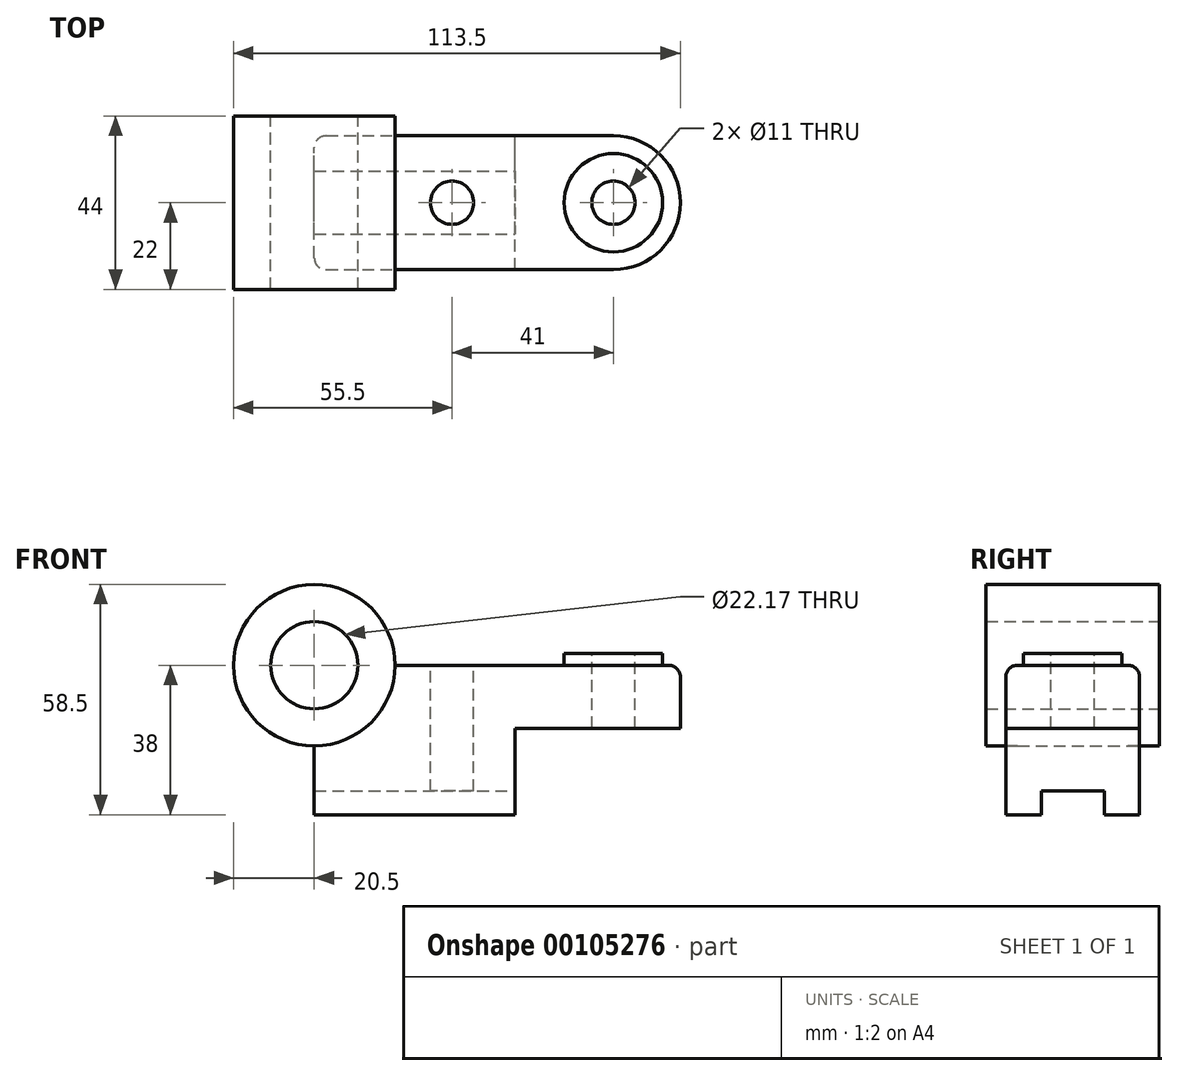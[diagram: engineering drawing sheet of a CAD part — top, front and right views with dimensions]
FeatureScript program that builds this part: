
annotation { "Feature Type Name" : "Feature", "Feature Type Description" : "" }
export const myFeature = defineFeature(function(context is Context, id is Id, definition is map)
    precondition{}
    {
        {
            var Q0;
            Q0=qCreatedBy(makeId("Front.planeOp"),FACE);
            var sketch = newSketch(context, id + "F0", { "sketchPlane" : qUnion([Q0])});
            skLineSegment(sketch, "E0.bottom", {"start": v(0, 0) * mm, "end": v(51, 0) * mm});
            skLineSegment(sketch, "E0.top", {"start": v(0, 38) * mm, "end": v(76, 38) * mm});
            skLineSegment(sketch, "E0.left", {"start": v(0, 0) * mm, "end": v(0, 38) * mm});
            skLineSegment(sketch, "E0.right", {"start": v(76, 22) * mm, "end": v(76, 38) * mm});
            skLineSegment(sketch, "E1.top", {"start": v(76, 22) * mm, "end": v(51, 22) * mm});
            skLineSegment(sketch, "E1.right", {"start": v(51, 0) * mm, "end": v(51, 22) * mm});
            skCircle(sketch, "E2", {"center": v(0, 38) * mm, "radius": 11.09 * mm});
            skCircle(sketch, "E3", {"center": v(0, 38) * mm, "radius": 20.5 * mm});
            skSolve(sketch);
        }
        {
            var Q0;
            {var subQ2=sQuery(id+"F0.wireOp",EDGE,"E0.bottom");Q0=makeQuery(id+"F0.imprint","IMPRINT",FACE,{"disambiguationData":[TD([[makeQuery(id+"F0.imprint","IMPRINT",EDGE,{"derivedFrom":subQ2}),1.0]])]});}
            extrude(context, id + "F1", {"entities" : qUnion([Q0]), "endBound" : BoundingType.SYMMETRIC, "depth" : (17 * 2) * mm});
        }
        {
            var Q0;
            {var subQ0=sQuery(id+"F0.wireOp",EDGE,"E3");var subQ1=sQuery(id+"F0.wireOp",EDGE,"E0.top");var subQ2=makeQuery(id+"F0.imprint","INTERSECT",VERTEX,{"derivedFrom":[subQ1,subQ0]});Q0=makeQuery(id+"F0.imprint","IMPRINT",FACE,{"disambiguationData":[TD([[makeQuery(id+"F0.imprint","IMPRINT",EDGE,{"disambiguationData":[TD([[subQ2,1.0]])],"derivedFrom":subQ1}),1.0]])]});}
            var Q1;
            {var subQ0=sQuery(id+"F0.wireOp",EDGE,"E3");var subQ1=sQuery(id+"F0.wireOp",EDGE,"E0.top");var subQ2=makeQuery(id+"F0.imprint","INTERSECT",VERTEX,{"derivedFrom":[subQ1,subQ0]});Q1=makeQuery(id+"F0.imprint","IMPRINT",FACE,{"disambiguationData":[TD([[makeQuery(id+"F0.imprint","IMPRINT",EDGE,{"disambiguationData":[TD([[subQ2,1.0]])],"derivedFrom":subQ1}),-1.0]])]});}
            extrude(context, id + "F2", {"entities" : qUnion([Q0, Q1]), "operationType" : NewBodyOperationType.ADD, "endBound" : BoundingType.SYMMETRIC, "depth" : 44 * mm});
        }
        {
            var Q0;
            Q0=makeQuery(id+"F1.opExtrude","SWEPT_FACE",FACE,{"disambiguationData":[OSD([sQuery(id+"F0.wireOp",EDGE,"E0.top")])]});
            var sketch = newSketch(context, id + "F3", { "sketchPlane" : qUnion([Q0])});
            skArc(sketch, "E4", {"start": v(76, -17) * mm, "mid": v(93, 0) * mm, "end": v(76, 17) * mm});
            skSolve(sketch);
        }
        {
            var Q0;
            Q0=makeQuery(id+"F3.imprint","IMPRINT",FACE,{"disambiguationData":[TD([[makeQuery(id+"F3.imprint","IMPRINT",EDGE,{"derivedFrom":sQuery(id+"F3.wireOp",EDGE,"E4")}),1.0]])]});
            var Q1;
            Q1=makeQuery(id+"F1.opExtrude","SWEPT_FACE",FACE,{"disambiguationData":[OSD([sQuery(id+"F0.wireOp",EDGE,"E1.top")])]});
            extrude(context, id + "F4", {"entities" : qUnion([Q0]), "operationType" : NewBodyOperationType.ADD, "endBound" : BoundingType.UP_TO_SURFACE, "oppositeDirection" : true, "endBoundEntityFace" : qUnion([Q1]), "depth" : 39.55 * mm});
        }
        {
            var Q0;
            {var subQ0=sQuery(id+"F0.wireOp",EDGE,"E0.top");Q0=makeQuery(id+"F4.boolean.opBoolean","MERGE",FACE,{"derivedFrom":[makeQuery(id+"F1.opExtrude","SWEPT_FACE",FACE,{"disambiguationData":[OSD([subQ0])]}),makeQuery(id+"F4.opExtrude","CAP_FACE",FACE,{"disambiguationData":[OSD([subQ0,sQuery(id+"F0.wireOp",EDGE,"E0.right"),sQuery(id+"F3.wireOp",EDGE,"E4")])],"isStart":true})]});}
            var sketch = newSketch(context, id + "F5", { "sketchPlane" : qUnion([Q0])});
            skCircle(sketch, "E5", {"center": v(76, 0) * mm, "radius": 12.5 * mm});
            skSolve(sketch);
        }
        {
            var Q0;
            Q0=makeQuery(id+"F5.imprint","IMPRINT",FACE,{"disambiguationData":[TD([[makeQuery(id+"F5.imprint","IMPRINT",EDGE,{"derivedFrom":sQuery(id+"F5.wireOp",EDGE,"E5")}),1.0]])]});
            extrude(context, id + "F6", {"entities" : qUnion([Q0]), "operationType" : NewBodyOperationType.ADD, "depth" : 3 * mm});
        }
        {
            var Q0;
            Q0=makeQuery(id+"F6.opExtrude","CAP_FACE",FACE,{"disambiguationData":[OSD([sQuery(id+"F5.wireOp",EDGE,"E5")])],"isStart":false});
            var sketch = newSketch(context, id + "F7", { "sketchPlane" : qUnion([Q0])});
            skCircle(sketch, "E6", {"center": v(76, 0) * mm, "radius": 5.5 * mm});
            skCircle(sketch, "E7", {"center": v(35, 0) * mm, "radius": 5.5 * mm});
            skSolve(sketch);
        }
        {
            var Q0;
            Q0 = qSketchRegion(id + "F7", true);
            extrude(context, id + "F8", {"entities" : qUnion([Q0]), "operationType" : NewBodyOperationType.REMOVE, "endBound" : BoundingType.THROUGH_ALL, "oppositeDirection" : true, "depth" : 49.88 * mm});
        }
        {
            var Q0;
            Q0=makeQuery(id+"F1.opExtrude","SWEPT_FACE",FACE,{"disambiguationData":[OSD([sQuery(id+"F0.wireOp",EDGE,"E1.right")])]});
            var sketch = newSketch(context, id + "F9", { "sketchPlane" : qUnion([Q0])});
            skLineSegment(sketch, "E8.bottom", {"start": v(8, 0) * mm, "end": v(-8, 0) * mm});
            skLineSegment(sketch, "E8.top", {"start": v(8, 6) * mm, "end": v(-8, 6) * mm});
            skLineSegment(sketch, "E8.left", {"start": v(8, 0) * mm, "end": v(8, 6) * mm});
            skLineSegment(sketch, "E8.right", {"start": v(-8, 0) * mm, "end": v(-8, 6) * mm});
            skSolve(sketch);
        }
        {
            var Q0;
            Q0 = qSketchRegion(id + "F9", true);
            extrude(context, id + "F10", {"entities" : qUnion([Q0]), "operationType" : NewBodyOperationType.REMOVE, "endBound" : BoundingType.THROUGH_ALL, "oppositeDirection" : true, "depth" : 25 * mm});
        }
        {
            var Q0;
            Q0=makeQuery(id+"F1.opExtrude","SWEPT_EDGE",EDGE,{"disambiguationData":[OSD([sQuery(id+"F0.wireOp",EDGE,"E0.top"),sQuery(id+"F0.wireOp",EDGE,"E3")])]});
            var Q1;
            Q1=makeQuery(id+"F1.opExtrude","CAP_EDGE",EDGE,{"disambiguationData":[OSD([sQuery(id+"F0.wireOp",EDGE,"E3")])],"isStart":false});
            var Q2;
            Q2=makeQuery(id+"F6.opExtrude","CAP_EDGE",EDGE,{"disambiguationData":[OSD([sQuery(id+"F5.wireOp",EDGE,"E5")])],"isStart":true});
            var Q3;
            Q3=makeQuery(id+"F1.opExtrude","CAP_EDGE",EDGE,{"disambiguationData":[OSD([sQuery(id+"F0.wireOp",EDGE,"E3")])],"isStart":true});
            var Q4;
            Q4=makeQuery(id+"F1.opExtrude","SWEPT_EDGE",EDGE,{"disambiguationData":[OSD([sQuery(id+"F0.wireOp",EDGE,"E0.left"),sQuery(id+"F0.wireOp",EDGE,"E3")])]});
            var Q5;
            Q5=makeQuery(id+"F1.opExtrude","CAP_EDGE",EDGE,{"disambiguationData":[OSD([sQuery(id+"F0.wireOp",EDGE,"E0.left")])],"isStart":true});
            var Q6;
            Q6=makeQuery(id+"F1.opExtrude","CAP_EDGE",EDGE,{"disambiguationData":[OSD([sQuery(id+"F0.wireOp",EDGE,"E0.left")])],"isStart":false});
            fillet(context, id + "F11", {"entities" : qUnion([Q0, Q1, Q2, Q3, Q4, Q5, Q6]), "radius" : 3 * mm, "tangentPropagation" : true, "allowEdgeOverflow" : false});
        }
        {
            var Q0;
            Q0=makeQuery(id+"F1.opExtrude","CAP_EDGE",EDGE,{"disambiguationData":[OSD([sQuery(id+"F0.wireOp",EDGE,"E0.top")])],"isStart":false});
            fillet(context, id + "F12", {"entities" : qUnion([Q0]), "radius" : 3 * mm, "tangentPropagation" : true, "allowEdgeOverflow" : false});
        }
    });
